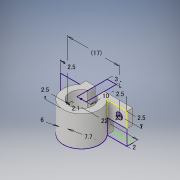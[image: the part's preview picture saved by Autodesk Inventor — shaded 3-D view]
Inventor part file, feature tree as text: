
AUTODESK INVENTOR PART (.ipt)
format: ipt  version: 2019.3 (Build 233278000, 278)  size: 158,720 bytes
history: native  units: mm
features: extrude x5, sketch x3, projected_geometry x2
ambient origin geometry x8: Origin, YZ Plane, XZ Plane, XY Plane, X Axis, Y Axis, Z Axis, Center Point
bodies: Body1 (feature_tree)
feature tree (10):
  sketch  "スケッチ3"
  extrude  "押し出し3"  Depth=7.7mm
  sketch  "スケッチ4"
  extrude  "押し出し4"  Depth=22.0mm
  sketch  "スケッチ5"
  extrude  "押し出し5"  Depth=2.0mm
  extrude  "押し出し6"  Depth=6.0mm
  extrude  "押し出し7"  Depth=10.0mm TaperAngle=0.0deg
  projected_geometry  "投影ループ1"
  projected_geometry  "投影ループ2"
